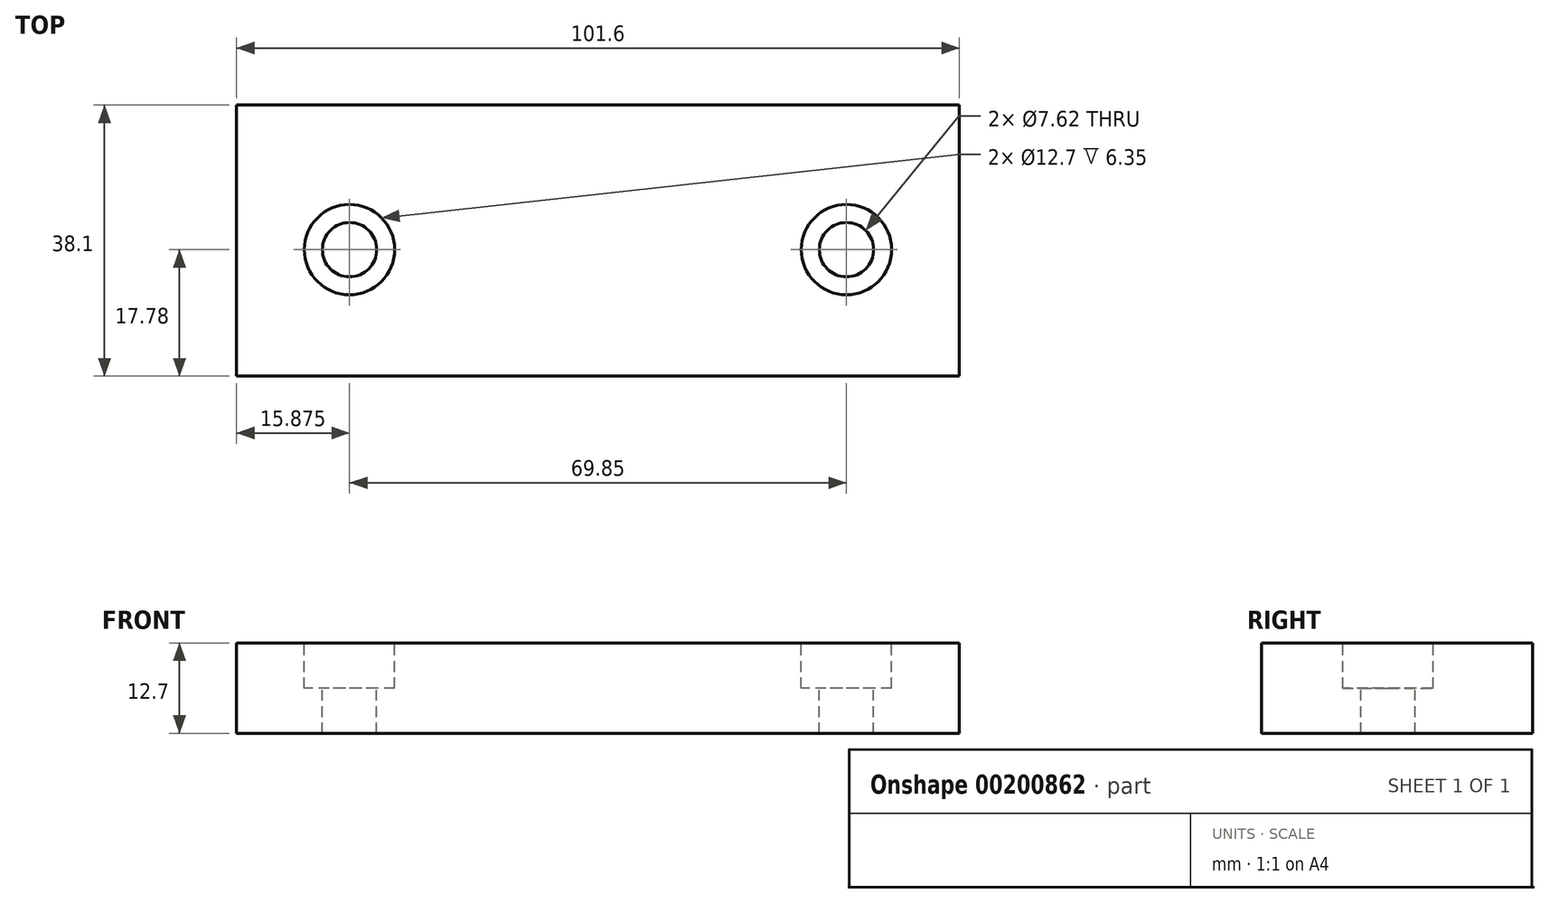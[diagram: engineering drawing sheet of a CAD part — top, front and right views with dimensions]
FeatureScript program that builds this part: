
annotation { "Feature Type Name" : "Feature", "Feature Type Description" : "" }
export const myFeature = defineFeature(function(context is Context, id is Id, definition is map)
    precondition{}
    {
        {
            var Q0;
            Q0=qCreatedBy(makeId("Top.planeOp"),FACE);
            var sketch = newSketch(context, id + "F0", { "sketchPlane" : qUnion([Q0])});
            skLineSegment(sketch, "E0.bottom", {"start": v(50.8, -19.05) * mm, "end": v(-50.8, -19.05) * mm});
            skLineSegment(sketch, "E0.top", {"start": v(50.8, 19.05) * mm, "end": v(-50.8, 19.05) * mm});
            skLineSegment(sketch, "E0.left", {"start": v(50.8, -19.05) * mm, "end": v(50.8, 19.05) * mm});
            skLineSegment(sketch, "E0.right", {"start": v(-50.8, -19.05) * mm, "end": v(-50.8, 19.05) * mm});
            skPoint(sketch, "E0.middle", {"position": v(0, 0) * mm});
            skLineSegment(sketch, "E1", {"start": v(0, 19.05) * mm, "end": v(0, -1.27) * mm});
            skLineSegment(sketch, "E2", {"start": v(0, -1.27) * mm, "end": v(34.93, -1.27) * mm});
            skLineSegment(sketch, "E3", {"start": v(0, -1.27) * mm, "end": v(-34.93, -1.27) * mm});
            skCircle(sketch, "E4", {"center": v(-34.93, -1.27) * mm, "radius": 6.35 * mm});
            skCircle(sketch, "E5", {"center": v(34.93, -1.27) * mm, "radius": 6.35 * mm});
            skCircle(sketch, "E6", {"center": v(-34.93, -1.27) * mm, "radius": 3.81 * mm});
            skCircle(sketch, "E7", {"center": v(34.93, -1.27) * mm, "radius": 3.81 * mm});
            skSolve(sketch);
        }
        {
            var Q0;
            Q0 = qSketchRegion(id + "F0", true);
            var Q1;
            Q1=makeQuery(id+"F0.imprint","IMPRINT",FACE,{"disambiguationData":[TD([[makeQuery(id+"F0.imprint","IMPRINT",EDGE,{"derivedFrom":sQuery(id+"F0.wireOp",EDGE,"E5")}),1.0]])]});
            var Q2;
            Q2=makeQuery(id+"F0.imprint","IMPRINT",FACE,{"disambiguationData":[TD([[makeQuery(id+"F0.imprint","IMPRINT",EDGE,{"derivedFrom":sQuery(id+"F0.wireOp",EDGE,"E4")}),1.0]])]});
            extrude(context, id + "F1", {"entities" : qUnion([Q0, Q1, Q2]), "oppositeDirection" : true, "depth" : 12.7 * mm});
        }
        {
            var Q0;
            Q0=makeQuery(id+"F0.imprint","IMPRINT",FACE,{"disambiguationData":[TD([[makeQuery(id+"F0.imprint","IMPRINT",EDGE,{"derivedFrom":sQuery(id+"F0.wireOp",EDGE,"E4")}),1.0]])]});
            var Q1;
            Q1=makeQuery(id+"F0.imprint","IMPRINT",FACE,{"disambiguationData":[TD([[makeQuery(id+"F0.imprint","IMPRINT",EDGE,{"derivedFrom":sQuery(id+"F0.wireOp",EDGE,"E5")}),1.0]])]});
            extrude(context, id + "F2", {"entities" : qUnion([Q0, Q1]), "operationType" : NewBodyOperationType.REMOVE, "oppositeDirection" : true, "depth" : 6.35 * mm});
        }
    });
